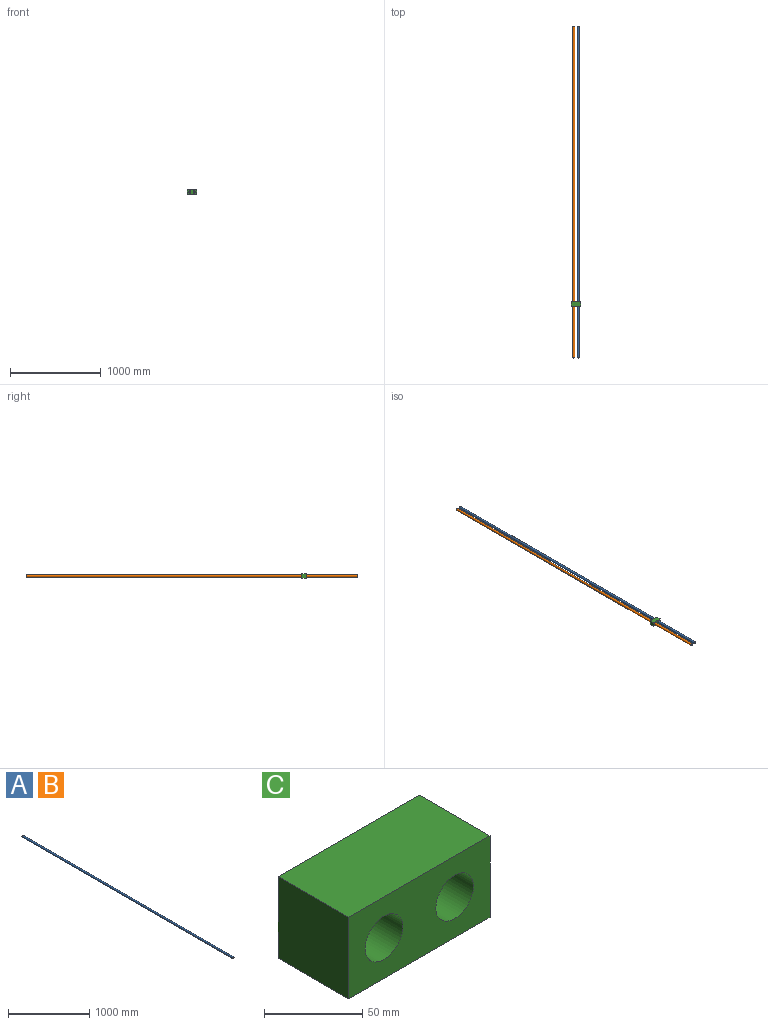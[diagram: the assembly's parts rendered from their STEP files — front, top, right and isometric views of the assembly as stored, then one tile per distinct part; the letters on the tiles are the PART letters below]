
ASSEMBLY  parts=3 mates=3
PART A: 4 faces, bbox 25.4x3657.6x25.4 mm
  f0: cylinder r=11.91mm len=3657.6mm, axis (0,-1,0), area 273622mm2, adj f2,f3
  f1: cylinder r=12.7mm len=3657.6mm, axis (0,-1,0), area 291863.5mm2, adj f2,f3
  f2: plane 25.4x25.4mm, normal (0,1,0), area 61.4mm2, adj f0,f1
  f3: plane 25.4x25.4mm, normal (0,-1,0), area 61.4mm2, adj f0,f1
PART B: same geometry as A
PART C: 8 faces, bbox 101.6x50.8x50.8 mm
  f0: plane 101.6x50.8mm, normal (0,0,1), area 5161.3mm2, adj f1,f5,f6,f7
  f1: plane 50.8x50.8mm, normal (-1,0,0), area 2580.6mm2, adj f0,f2,f6,f7
  f2: plane 101.6x50.8mm, normal (0,0,-1), area 5161.3mm2, adj f1,f5,f6,f7
  f3: cylinder r=13.49mm len=50.8mm, axis (0,-1,0), area 4307mm2, adj f6,f7
  f4: cylinder r=13.49mm len=50.8mm, axis (0,-1,0), area 4307mm2, adj f6,f7
  f5: plane 50.8x50.8mm, normal (1,0,0), area 2580.6mm2, adj f0,f2,f6,f7
  f6: plane 101.6x50.8mm, normal (0,1,0), area 4017.2mm2, adj f0,f1,f2,f3,f4,f5
  f7: plane 101.6x50.8mm, normal (0,-1,0), area 4017.2mm2, adj f0,f1,f2,f3,f4,f5
PLACE A t=(50.8,0,0)mm
PLACE B at identity fixed
PLACE C t=(0,569.46,0)mm
MATE slider C.f3 <-> B.f0  axis (0,-1,0) through (0,594.86,0)mm
MATE planar A.f1 <-> B.f1  axis (0,-1,0) through (50.8,0,0)mm
MATE slider A.f1 <-> C.f4  axis (0,-1,0) through (50.8,0,0)mm
